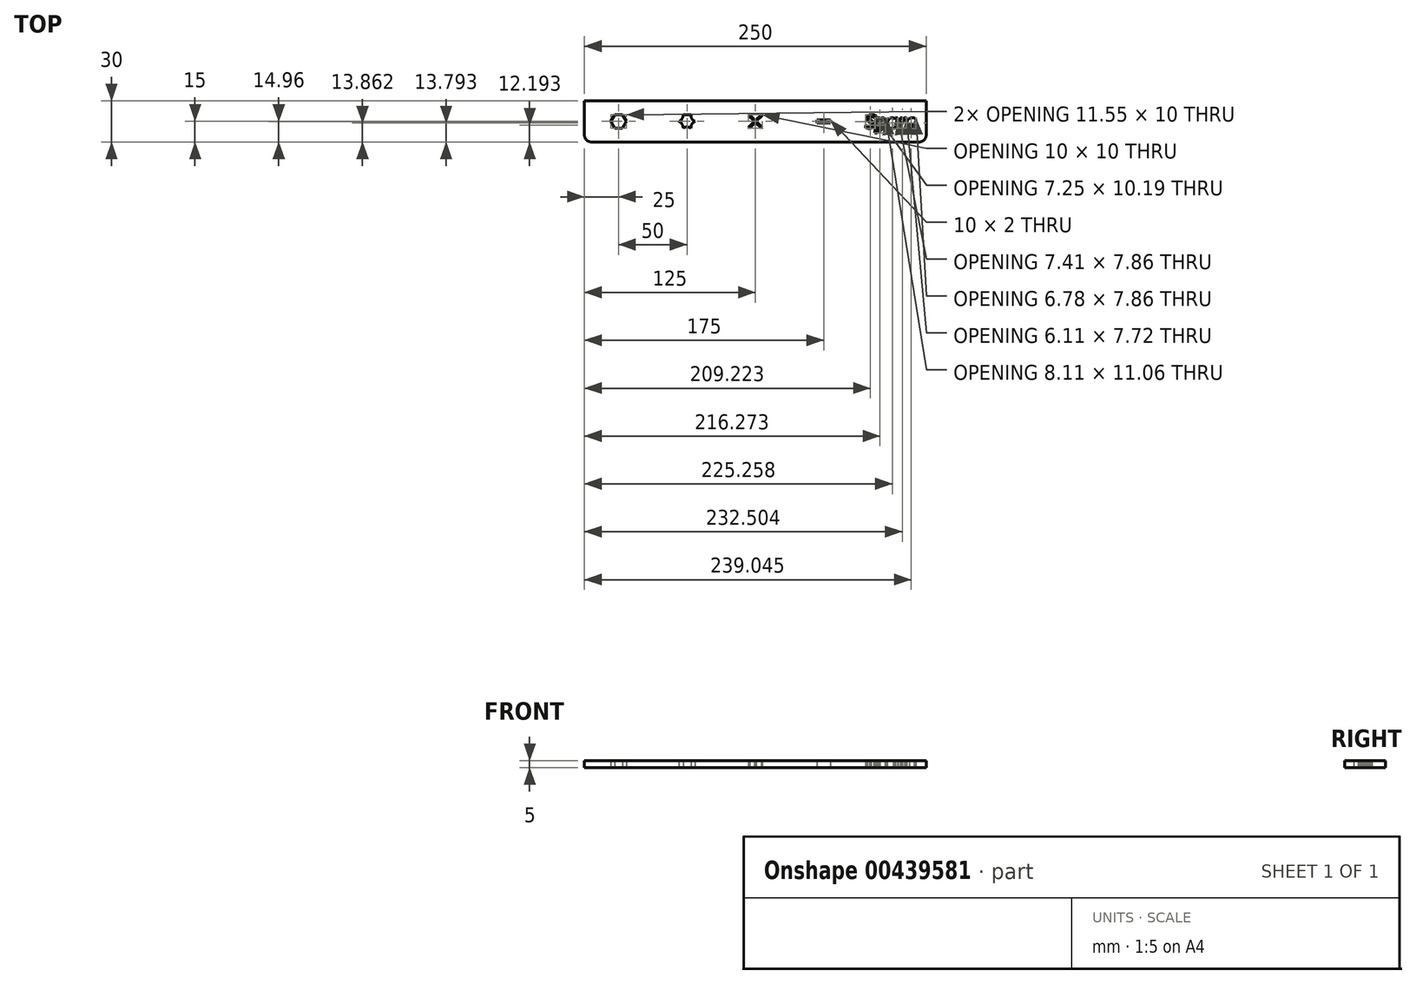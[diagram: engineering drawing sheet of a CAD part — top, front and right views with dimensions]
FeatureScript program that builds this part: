
annotation { "Feature Type Name" : "Feature", "Feature Type Description" : "" }
export const myFeature = defineFeature(function(context is Context, id is Id, definition is map)
    precondition{}
    {
        {
            var Q0;
            Q0=qCreatedBy(makeId("Top.planeOp"),FACE);
            var sketch = newSketch(context, id + "F0", { "sketchPlane" : qUnion([Q0])});
            skLineSegment(sketch, "E0.bottom", {"start": v(-125, 15) * mm, "end": v(125, 15) * mm});
            skLineSegment(sketch, "E0.top", {"start": v(-125, -15) * mm, "end": v(125, -15) * mm});
            skLineSegment(sketch, "E0.left", {"start": v(-125, 15) * mm, "end": v(-125, -15) * mm});
            skLineSegment(sketch, "E0.right", {"start": v(125, 15) * mm, "end": v(125, -15) * mm});
            skPoint(sketch, "E0.middle", {"position": v(0, 0) * mm});
            skPoint(sketch, "E1", {"position": v(-100, 0) * mm});
            skPoint(sketch, "E2", {"position": v(-50, 0) * mm});
            skPoint(sketch, "E3", {"position": v(50, 0) * mm});
            skPoint(sketch, "E4", {"position": v(100, 0) * mm});
            skLineSegment(sketch, "E5", {"start": v(-125, 5) * mm, "end": v(125, 5) * mm});
            skLineSegment(sketch, "E6", {"start": v(-125, -5) * mm, "end": v(125, -5) * mm, "construction": true});
            skCircle(sketch, "E7.cCircle", {"center": v(-100, 0) * mm, "radius": 5 * mm, "construction": true});
            skLineSegment(sketch, "E7.0", {"start": v(-105.77, 0) * mm, "end": v(-102.89, 5) * mm});
            skLineSegment(sketch, "E7.1", {"start": v(-102.89, 5) * mm, "end": v(-97.11, 5) * mm});
            skLineSegment(sketch, "E7.2", {"start": v(-97.11, 5) * mm, "end": v(-94.23, 0) * mm});
            skLineSegment(sketch, "E7.3", {"start": v(-94.23, 0) * mm, "end": v(-97.11, -5) * mm});
            skLineSegment(sketch, "E7.4", {"start": v(-97.11, -5) * mm, "end": v(-102.89, -5) * mm});
            skLineSegment(sketch, "E7.5", {"start": v(-102.89, -5) * mm, "end": v(-105.77, 0) * mm});
            skPoint(sketch, "E7.0.midPoint", {"position": v(-104.33, 2.5) * mm});
            skCircle(sketch, "E8.cCircle", {"center": v(-50, 0) * mm, "radius": 5 * mm, "construction": true});
            skPoint(sketch, "E8.cCircle.perimeterSnap0", {"position": v(-100, 5) * mm});
            skLineSegment(sketch, "E8.0", {"start": v(-52.89, 5) * mm, "end": v(-47.11, 5) * mm});
            skLineSegment(sketch, "E8.1", {"start": v(-47.11, 5) * mm, "end": v(-44.23, 0) * mm, "construction": true});
            skLineSegment(sketch, "E8.2", {"start": v(-44.23, 0) * mm, "end": v(-47.11, -5) * mm, "construction": true});
            skLineSegment(sketch, "E8.3", {"start": v(-47.11, -5) * mm, "end": v(-52.89, -5) * mm});
            skLineSegment(sketch, "E8.4", {"start": v(-52.89, -5) * mm, "end": v(-55.77, 0) * mm, "construction": true});
            skLineSegment(sketch, "E8.5", {"start": v(-55.77, 0) * mm, "end": v(-52.89, 5) * mm, "construction": true});
            skPoint(sketch, "E8.0.midPoint", {"position": v(-50, 5) * mm});
            skPoint(sketch, "E8.0.midPoint.positionSnap0", {"position": v(-100, 5) * mm});
            skLineSegment(sketch, "E9.bottom", {"start": v(-5, 5) * mm, "end": v(5, 5) * mm});
            skLineSegment(sketch, "E9.top", {"start": v(-5, -5) * mm, "end": v(5, -5) * mm});
            skLineSegment(sketch, "E9.left", {"start": v(-5, 5) * mm, "end": v(-5, -5) * mm, "construction": true});
            skLineSegment(sketch, "E9.right", {"start": v(5, 5) * mm, "end": v(5, -5) * mm, "construction": true});
            skLineSegment(sketch, "E10", {"start": v(5, 5) * mm, "end": v(-5, -5) * mm, "construction": true});
            skLineSegment(sketch, "E11", {"start": v(-5, 5) * mm, "end": v(5, -5) * mm, "construction": true});
            skLineSegment(sketch, "E12", {"start": v(0, 5) * mm, "end": v(0, -5) * mm, "construction": true});
            skLineSegment(sketch, "E13", {"start": v(-5, 0) * mm, "end": v(5, 0) * mm, "construction": true});
            skArc(sketch, "E14", {"start": v(-55.77, 0) * mm, "mid": v(-53.54, 2.04) * mm, "end": v(-52.89, 5) * mm});
            skArc(sketch, "E15", {"start": v(-52.89, 5) * mm, "mid": v(-50, 4.08) * mm, "end": v(-47.11, 5) * mm});
            skArc(sketch, "E16", {"start": v(-47.11, 5) * mm, "mid": v(-46.46, 2.04) * mm, "end": v(-44.23, 0) * mm});
            skArc(sketch, "E17", {"start": v(-44.23, 0) * mm, "mid": v(-46.46, -2.04) * mm, "end": v(-47.11, -5) * mm});
            skArc(sketch, "E18", {"start": v(-47.11, -5) * mm, "mid": v(-50, -4.08) * mm, "end": v(-52.89, -5) * mm});
            skArc(sketch, "E19", {"start": v(-52.89, -5) * mm, "mid": v(-53.54, -2.04) * mm, "end": v(-55.77, 0) * mm});
            skLineSegment(sketch, "E20.bottom", {"start": v(45, 1) * mm, "end": v(55, 1) * mm});
            skLineSegment(sketch, "E20.top", {"start": v(45, -1) * mm, "end": v(55, -1) * mm});
            skLineSegment(sketch, "E20.left", {"start": v(45, 1) * mm, "end": v(45, -1) * mm});
            skLineSegment(sketch, "E20.right", {"start": v(55, 1) * mm, "end": v(55, -1) * mm});
            skText(sketch, "E21", { "text": "Spare", "fontName": "OpenSans-BoldItalic.ttf"});
            skLineSegment(sketch, "E22", {"start": v(5, 4.3) * mm, "end": v(-4.3, -5) * mm});
            skLineSegment(sketch, "E23", {"start": v(-4.24, 5) * mm, "end": v(5, -4.24) * mm});
            skLineSegment(sketch, "E24", {"start": v(-5, 4.3) * mm, "end": v(4.3, -5) * mm});
            skLineSegment(sketch, "E25", {"start": v(-5, -4.3) * mm, "end": v(4.3, 5) * mm});
            skLineSegment(sketch, "E26", {"start": v(-4.24, 5) * mm, "end": v(-5, 4.3) * mm});
            skLineSegment(sketch, "E27", {"start": v(4.3, 5) * mm, "end": v(5, 4.3) * mm});
            skLineSegment(sketch, "E28", {"start": v(5, -4.24) * mm, "end": v(4.3, -5) * mm});
            skLineSegment(sketch, "E29", {"start": v(-4.3, -5) * mm, "end": v(-5, -4.3) * mm});
            const initialGuessF0  = {"E21": [0.08032, -0.005, 1, 0, 0.01]};
            skSetInitialGuess(sketch, initialGuessF0);
            skSolve(sketch);
        }
        {
            var Q0;
            Q0 = qSketchRegion(id + "F0", true);
            var Q1;
            {var subQ0=sQuery(id+"F0.wireOp",EDGE,"E23");var subQ3=sQuery(id+"F0.wireOp",EDGE,"E25");var subQ5=makeQuery(id+"F0.imprint","INTERSECT",VERTEX,{"derivedFrom":[subQ0,subQ3]});Q1=makeQuery(id+"F0.imprint","IMPRINT",FACE,{"disambiguationData":[TD([[makeQuery(id+"F0.imprint","IMPRINT",EDGE,{"disambiguationData":[TD([[subQ5,1.0]])],"derivedFrom":subQ0}),1.0]])]});}
            var Q2;
            {var subQ0=sQuery(id+"F0.wireOp",EDGE,"E22");var subQ3=sQuery(id+"F0.wireOp",EDGE,"E24");var subQ5=makeQuery(id+"F0.imprint","INTERSECT",VERTEX,{"derivedFrom":[subQ0,subQ3]});Q2=makeQuery(id+"F0.imprint","IMPRINT",FACE,{"disambiguationData":[TD([[makeQuery(id+"F0.imprint","IMPRINT",EDGE,{"disambiguationData":[TD([[subQ5,-1.0]])],"derivedFrom":subQ0}),1.0]])]});}
            var Q3;
            Q3=makeQuery(id+"F0.imprint","IMPRINT",FACE,{"disambiguationData":[TD([[makeQuery(id+"F0.imprint","IMPRINT",EDGE,{"derivedFrom":sQuery(id+"F0.wireOp",EDGE,"E8.0")}),-1.0]])]});
            var Q4;
            Q4=makeQuery(id+"F0.imprint","IMPRINT",FACE,{"disambiguationData":[TD([[makeQuery(id+"F0.imprint","IMPRINT",EDGE,{"derivedFrom":sQuery(id+"F0.wireOp",EDGE,"E8.3")}),-1.0]])]});
            extrude(context, id + "F1", {"entities" : qUnion([Q0, Q1, Q2, Q3, Q4]), "depth" : 5 * mm});
        }
        {
            var Q0;
            Q0=makeQuery(id+"F1.opExtrude","SWEPT_EDGE",EDGE,{"disambiguationData":[OSD([sQuery(id+"F0.wireOp",EDGE,"E0.top"),sQuery(id+"F0.wireOp",EDGE,"E0.left")])]});
            var Q1;
            Q1=makeQuery(id+"F1.opExtrude","SWEPT_EDGE",EDGE,{"disambiguationData":[OSD([sQuery(id+"F0.wireOp",EDGE,"E0.top"),sQuery(id+"F0.wireOp",EDGE,"E0.right")])]});
            fillet(context, id + "F2", {"entities" : qUnion([Q0, Q1]), "radius" : 5 * mm, "tangentPropagation" : true, "allowEdgeOverflow" : false});
        }
    });
